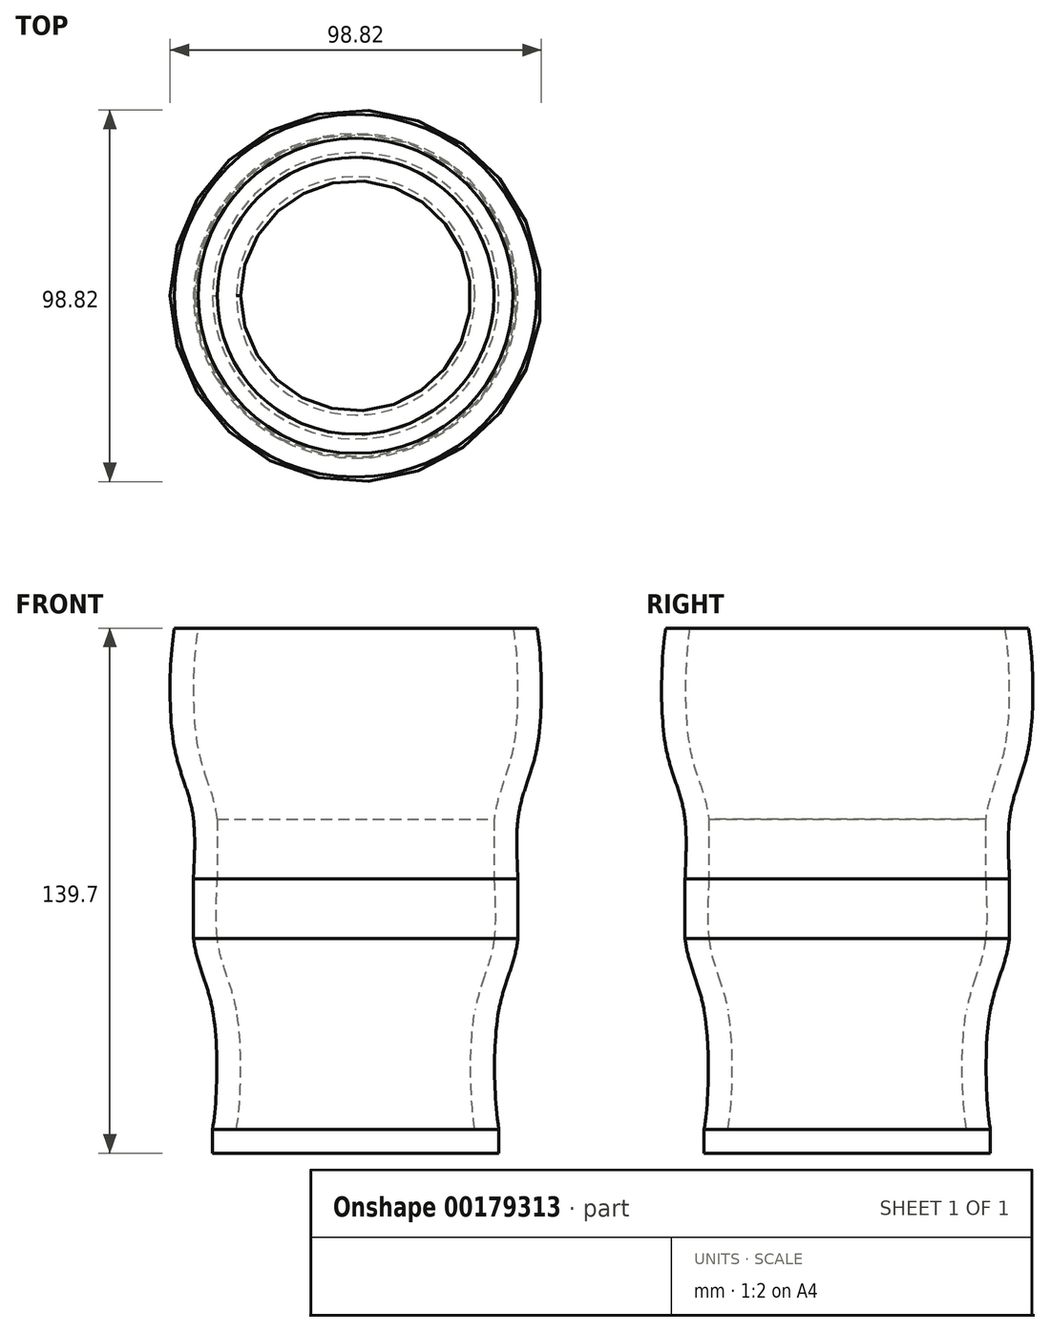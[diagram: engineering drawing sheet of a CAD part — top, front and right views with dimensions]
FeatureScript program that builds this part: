
annotation { "Feature Type Name" : "Feature", "Feature Type Description" : "" }
export const myFeature = defineFeature(function(context is Context, id is Id, definition is map)
    precondition{}
    {
        {
            var Q0;
            Q0=qCreatedBy(makeId("Top.planeOp"),FACE);
            var sketch = newSketch(context, id + "F0", { "sketchPlane" : qUnion([Q0])});
            skCircle(sketch, "E0", {"center": v(0, 0) * mm, "radius": 31.75 * mm});
            skCircle(sketch, "E1", {"center": v(0, 0) * mm, "radius": 38.1 * mm});
            skLineSegment(sketch, "E2", {"start": v(38.1, 0) * mm, "end": v(31.75, 0) * mm});
            skSolve(sketch);
        }
        {
            var Q0;
            Q0=qCreatedBy(makeId("Front.planeOp"),FACE);
            var sketch = newSketch(context, id + "F1", { "sketchPlane" : qUnion([Q0])});
            skLineSegment(sketch, "E3", {"start": v(38.1, 0) * mm, "end": v(38.1, 31.75) * mm});
            skLineSegment(sketch, "E4", {"start": v(38.1, 31.75) * mm, "end": v(40.64, 31.75) * mm});
            skLineSegment(sketch, "E5", {"start": v(40.64, 31.75) * mm, "end": v(40.64, 50.8) * mm});
            skLineSegment(sketch, "E6", {"start": v(40.64, 50.8) * mm, "end": v(43.18, 50.8) * mm});
            skLineSegment(sketch, "E7", {"start": v(43.18, 50.8) * mm, "end": v(43.18, 82.55) * mm});
            skLineSegment(sketch, "E8", {"start": v(43.18, 82.55) * mm, "end": v(45.72, 82.55) * mm});
            skLineSegment(sketch, "E9", {"start": v(45.72, 82.55) * mm, "end": v(45.72, 101.6) * mm});
            skLineSegment(sketch, "E10", {"start": v(45.72, 101.6) * mm, "end": v(48.26, 101.6) * mm});
            skLineSegment(sketch, "E11", {"start": v(48.26, 101.6) * mm, "end": v(48.26, 133.35) * mm});
            skFitSpline(sketch, "E12", {"points": [v(38.1, 0) * mm, v(38.1, 31.75) * mm, v(43.18, 50.8) * mm, v(43.18, 82.55) * mm, v(48.26, 101.6) * mm, v(48.26, 133.35) * mm], "startDerivative": vector(-17.42, 99.82) * mm, "endDerivative": vector(-17.42, 99.82) * mm});
            skLineSegment(sketch, "E13", {"start": v(31.75, -0.06) * mm, "end": v(31.75, 31.7) * mm});
            skLineSegment(sketch, "E14", {"start": v(31.75, 31.7) * mm, "end": v(34.3, 31.7) * mm});
            skLineSegment(sketch, "E15", {"start": v(34.3, 31.7) * mm, "end": v(34.3, 50.74) * mm});
            skLineSegment(sketch, "E16", {"start": v(34.3, 50.74) * mm, "end": v(36.83, 50.74) * mm});
            skLineSegment(sketch, "E17", {"start": v(36.83, 50.74) * mm, "end": v(36.83, 82.5) * mm});
            skLineSegment(sketch, "E18", {"start": v(36.83, 82.5) * mm, "end": v(39.37, 82.5) * mm});
            skLineSegment(sketch, "E19", {"start": v(39.37, 82.5) * mm, "end": v(39.37, 101.54) * mm});
            skLineSegment(sketch, "E20", {"start": v(39.37, 101.54) * mm, "end": v(41.91, 101.54) * mm});
            skLineSegment(sketch, "E21", {"start": v(41.91, 101.54) * mm, "end": v(41.91, 133.3) * mm});
            skFitSpline(sketch, "E22", {"points": [v(31.75, -0.06) * mm, v(31.75, 31.7) * mm, v(36.83, 50.74) * mm, v(36.83, 82.5) * mm, v(41.91, 101.54) * mm, v(41.91, 133.3) * mm], "startDerivative": vector(-17.42, 99.82) * mm, "endDerivative": vector(-17.42, 99.82) * mm});
            skLineSegment(sketch, "E23", {"start": v(41.91, 133.3) * mm, "end": v(48.26, 133.35) * mm});
            skLineSegment(sketch, "E24", {"start": v(38.1, 0) * mm, "end": v(31.75, -0.06) * mm});
            skSolve(sketch);
        }
        {
            var Q0;
            {var subQ4=sQuery(id+"F1.wireOp",EDGE,"E6");Q0=makeQuery(id+"F1.imprint","IMPRINT",FACE,{"disambiguationData":[TD([[makeQuery(id+"F1.imprint","IMPRINT",EDGE,{"derivedFrom":subQ4}),1.0]])]});}
            var Q1;
            {var subQ0=sQuery(id+"F1.wireOp",EDGE,"E18");Q1=makeQuery(id+"F1.imprint","IMPRINT",FACE,{"disambiguationData":[TD([[makeQuery(id+"F1.imprint","IMPRINT",EDGE,{"derivedFrom":subQ0}),1.0]])]});}
            var Q2;
            {var subQ0=sQuery(id+"F1.wireOp",EDGE,"E10");Q2=makeQuery(id+"F1.imprint","IMPRINT",FACE,{"disambiguationData":[TD([[makeQuery(id+"F1.imprint","IMPRINT",EDGE,{"derivedFrom":subQ0}),-1.0]])]});}
            var Q3;
            {var subQ0=sQuery(id+"F1.wireOp",EDGE,"E6");Q3=makeQuery(id+"F1.imprint","IMPRINT",FACE,{"disambiguationData":[TD([[makeQuery(id+"F1.imprint","IMPRINT",EDGE,{"derivedFrom":subQ0}),-1.0]])]});}
            var Q4;
            {var subQ0=sQuery(id+"F1.wireOp",EDGE,"E14");Q4=makeQuery(id+"F1.imprint","IMPRINT",FACE,{"disambiguationData":[TD([[makeQuery(id+"F1.imprint","IMPRINT",EDGE,{"derivedFrom":subQ0}),1.0]])]});}
            var Q5;
            {var subQ0=sQuery(id+"F1.wireOp",EDGE,"E13");Q5=makeQuery(id+"F1.imprint","IMPRINT",FACE,{"disambiguationData":[TD([[makeQuery(id+"F1.imprint","IMPRINT",EDGE,{"derivedFrom":subQ0}),1.0]])]});}
            var Q6;
            {var subQ0=sQuery(id+"F1.wireOp",EDGE,"E11");Q6=makeQuery(id+"F1.imprint","IMPRINT",FACE,{"disambiguationData":[TD([[makeQuery(id+"F1.imprint","IMPRINT",EDGE,{"derivedFrom":subQ0}),-1.0]])]});}
            var Q7;
            Q7=sQuery(id+"F0.wireOp",EDGE,"E0");
            revolve(context, id + "F2", {"entities" : qUnion([Q0, Q1, Q2, Q3, Q4, Q5, Q6]), "axis" : qUnion([Q7]), "revolveType" : RevolveType.FULL});
        }
        {
            var Q0;
            Q0=makeQuery(id+"F0.imprint","IMPRINT",FACE,{"disambiguationData":[TD([[makeQuery(id+"F0.imprint","IMPRINT",EDGE,{"derivedFrom":sQuery(id+"F0.wireOp",EDGE,"E0")}),1.0]])]});
            var Q1;
            Q1=makeQuery(id+"F0.imprint","IMPRINT",FACE,{"disambiguationData":[TD([[makeQuery(id+"F0.imprint","IMPRINT",EDGE,{"derivedFrom":sQuery(id+"F0.wireOp",EDGE,"E0")}),-1.0]])]});
            extrude(context, id + "F3", {"entities" : qUnion([Q0, Q1]), "operationType" : NewBodyOperationType.ADD, "oppositeDirection" : true, "depth" : 6.35 * mm});
        }
    });
